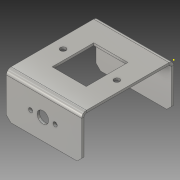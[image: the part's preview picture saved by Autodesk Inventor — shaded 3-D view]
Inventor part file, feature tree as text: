
AUTODESK INVENTOR PART (.ipt)
format: ipt  version: 2016 SP1 (Build 200210100, 210)  size: 163,328 bytes
history: native  units: in
note: dims shown in document units (in); Inventor stores cm internally (conversion verified against a paired STEP export)
features: sketch x7, sheet_metal_op x4, hole x4, other x4
ambient origin geometry x8: Origin, YZ Plane, XZ Plane, XY Plane, X Axis, Y Axis, Z Axis, Center Point
bodies: Solid1 (feature_tree)
feature tree (19):
  sheet_metal_op  "Face1"
  sheet_metal_op  "Flange1"
  hole  "Hole1"  [1 undecoded]
  sketch  "Sketch5"  dims[d10=0.2564in]
  hole  "Hole2"  [1 undecoded]
  hole  "Hole3"  [1 undecoded]
  sketch  "Sketch6"  dims[d11=0.0641in]
  hole  "Hole4"  [1 undecoded]
  other  "Corner Chamfer1"
  sketch  "Sketch1"  dims[d0=2.06in d1=2.515in]
  other  "Plate1"
  sketch  "Sketch2"  dims[d2=0.0641in d3=0.0641in]
  other  "Plate2"
  sheet_metal_op  "Bend1"
  sheet_metal_op  "Corner1"
  sketch  "Sketch3"  dims[d4=0.0321in d5=0.1282in]
  sketch  "Sketch4"  dims[d6=0.0641in d7=1.2in d8=90.0deg d9=0.0641in]
  sketch  "Sketch7"  dims[d12=0.0641in d13=0.688in d14=1.827in d15=0.563in d16=1.497in d17=0.0641in d18=0.0in d19=0.295in d20=1.765in d21=0.153in d22=0.75in d23=0.375in d24=0.25in d25=0.5635in d26=0.0641in d27=0.8108in d28=0.631in d29=0.665in d30=1.0in d31=1.335in d32=0.116in d33=0.75in d34=0.375in d35=0.25in d36=0.5635in d37=0.0641in d38=0.8108in d39=0.315in d40=0.75in d41=0.375in d42=0.25in d43=0.5635in d44=0.0641in d45=0.8108in d46=0.17in d47=0.75in d48=0.375in d49=0.25in d50=0.5635in d51=0.0641in d52=0.8108in d53=0.125in d54=0.25in d55=45.0deg]
  other  "Cut1"
note: 4 required parameter values undecoded (feature->parameter linkage not recoverable at this tier; creation-order binding heuristic only, values carry confidence <= 0.55)
